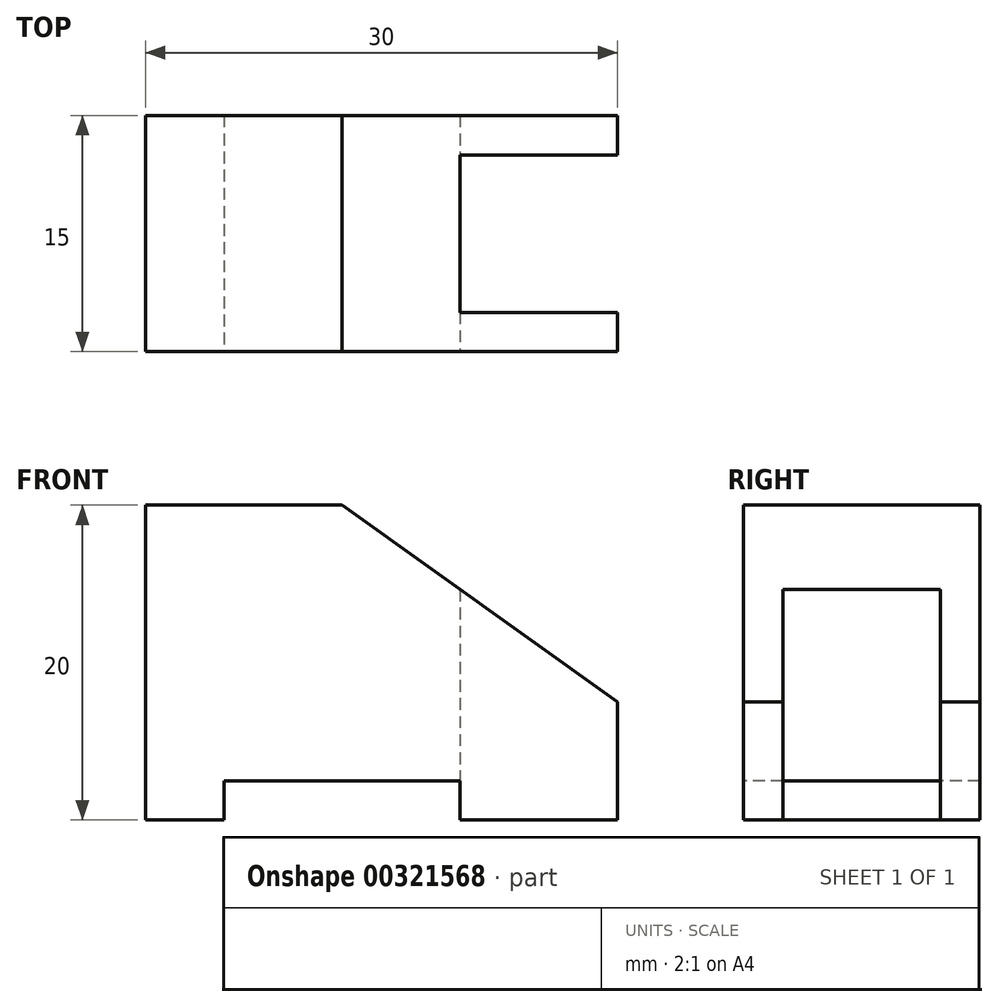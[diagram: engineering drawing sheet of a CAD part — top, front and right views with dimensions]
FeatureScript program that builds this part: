
annotation { "Feature Type Name" : "Feature", "Feature Type Description" : "" }
export const myFeature = defineFeature(function(context is Context, id is Id, definition is map)
    precondition{}
    {
        {
            var Q0;
            Q0=qCreatedBy(makeId("Front.planeOp"),FACE);
            var sketch = newSketch(context, id + "F0", { "sketchPlane" : qUnion([Q0])});
            skLineSegment(sketch, "E0", {"start": v(0, 0) * mm, "end": v(0, 20) * mm});
            skLineSegment(sketch, "E1", {"start": v(0, 20) * mm, "end": v(12.5, 20) * mm});
            skLineSegment(sketch, "E2", {"start": v(12.5, 20) * mm, "end": v(30, 7.5) * mm});
            skLineSegment(sketch, "E3", {"start": v(30, 7.5) * mm, "end": v(30, 0) * mm});
            skLineSegment(sketch, "E4", {"start": v(30, 0) * mm, "end": v(20, 0) * mm});
            skLineSegment(sketch, "E5", {"start": v(20, 0) * mm, "end": v(20, 2.5) * mm});
            skLineSegment(sketch, "E6", {"start": v(20, 2.5) * mm, "end": v(5, 2.5) * mm});
            skLineSegment(sketch, "E7", {"start": v(5, 2.5) * mm, "end": v(5, 0) * mm});
            skLineSegment(sketch, "E8", {"start": v(5, 0) * mm, "end": v(0, 0) * mm});
            skSolve(sketch);
        }
        {
            var Q0;
            Q0=makeQuery(id+"F0.imprint","IMPRINT",FACE,{"disambiguationData":[TD([[makeQuery(id+"F0.imprint","IMPRINT",EDGE,{"derivedFrom":sQuery(id+"F0.wireOp",EDGE,"E0")}),-1.0]])]});
            extrude(context, id + "F1", {"entities" : qUnion([Q0]), "endBound" : BoundingType.SYMMETRIC, "oppositeDirection" : true, "depth" : 15 * mm});
        }
        {
            var Q0;
            Q0=qCreatedBy(makeId("Top.planeOp"),FACE);
            var sketch = newSketch(context, id + "F2", { "sketchPlane" : qUnion([Q0])});
            skLineSegment(sketch, "E9.bottom", {"start": v(20, 5) * mm, "end": v(30, 5) * mm});
            skLineSegment(sketch, "E9.top", {"start": v(20, -5) * mm, "end": v(30, -5) * mm});
            skLineSegment(sketch, "E9.left", {"start": v(20, 5) * mm, "end": v(20, -5) * mm});
            skLineSegment(sketch, "E9.right", {"start": v(30, 5) * mm, "end": v(30, -5) * mm});
            skSolve(sketch);
        }
        {
            var Q0;
            Q0 = qSketchRegion(id + "F2", true);
            extrude(context, id + "F3", {"entities" : qUnion([Q0]), "operationType" : NewBodyOperationType.REMOVE, "endBound" : BoundingType.THROUGH_ALL, "depth" : 25 * mm});
        }
    });
